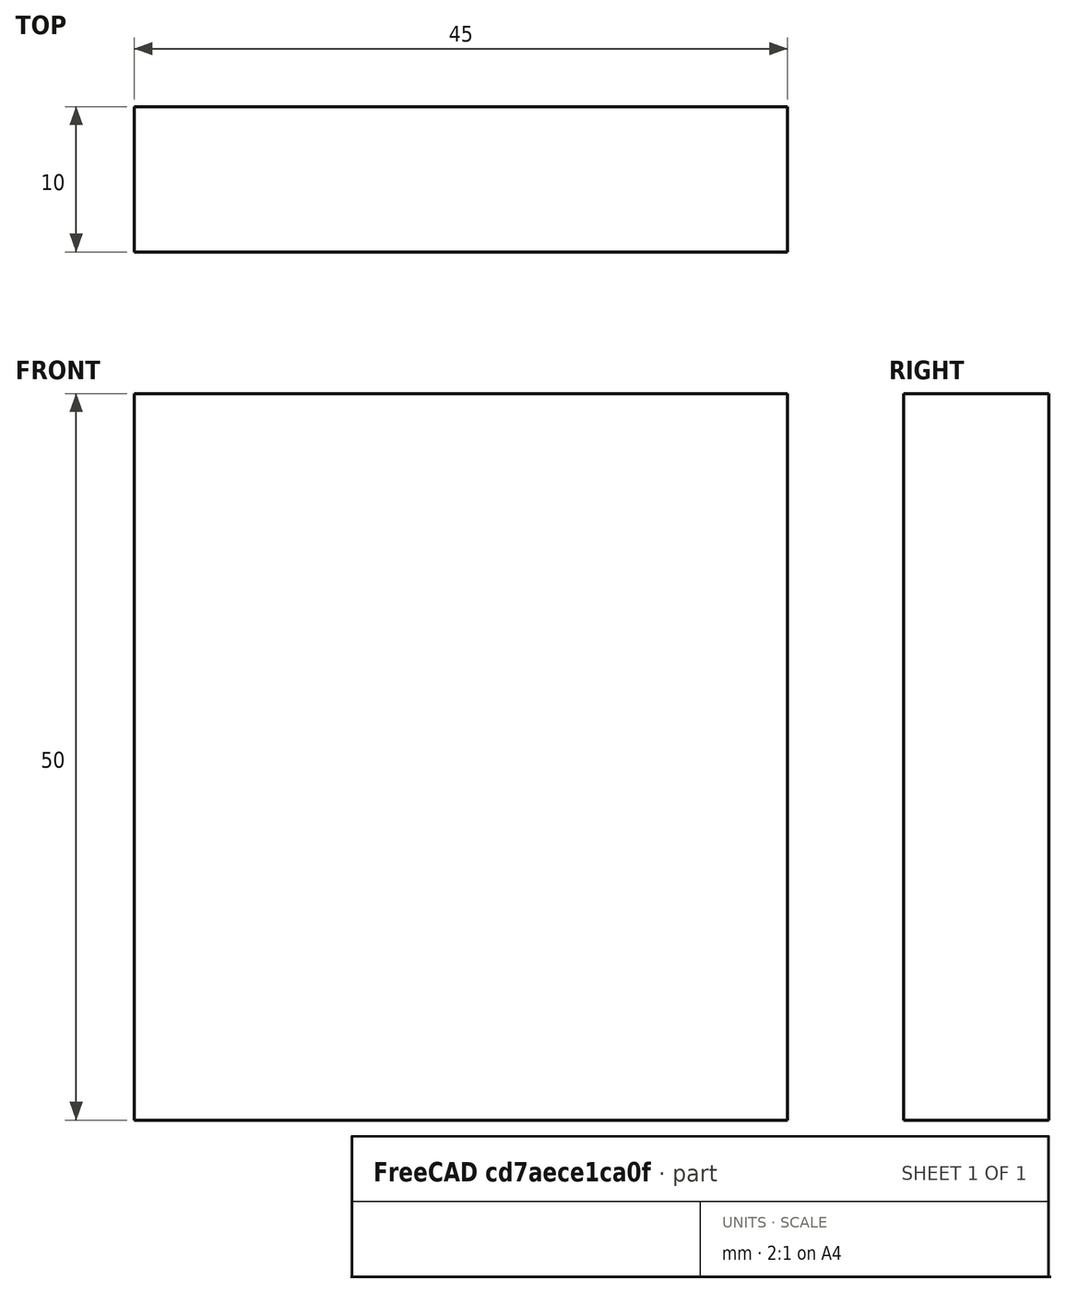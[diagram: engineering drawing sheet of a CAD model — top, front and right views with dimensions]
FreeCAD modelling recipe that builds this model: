
FCSTD DOCUMENT  (FreeCAD 0.15R4671 (Git))
Label: Flat Bar 45x10 EN10058 S235JR
License: All rights reserved
LicenseURL: http://en.wikipedia.org/wiki/All_rights_reserved
objects: Sketcher::SketchObject×1, Part::Extrusion×1
note: 2 computed .brp shape members not serialized (recipe doc carries the construction recipe); baked Part::Feature solids carry a one-line shape summary decoded from their .brp

FEATURE [Sketcher::SketchObject] Sketch
  sketch-geometry (4):
    g0: LineSegment StartX=-22.5 StartY=-5 StartZ=0 EndX=22.5 EndY=-5 EndZ=0
    g1: LineSegment StartX=22.5 StartY=-5 StartZ=0 EndX=22.5 EndY=5 EndZ=0
    g2: LineSegment StartX=22.5 StartY=5 StartZ=0 EndX=-22.5 EndY=5 EndZ=0
    g3: LineSegment StartX=-22.5 StartY=5 StartZ=0 EndX=-22.5 EndY=-5 EndZ=0
  constraints (12):
    c: Coincident(g0,g1)
    c: Coincident(g1,g2)
    c: Coincident(g2,g3)
    c: Coincident(g3,g0)
    c: Horizontal(g0)
    c: Horizontal(g2)
    c: Vertical(g1)
    c: Vertical(g3)
    c: Symmetric(g1,g2,g-2)
    c: Symmetric(g0,g1,g-1)
    c: DistanceY(g1) = 10
    c: DistanceX(g0) = 45
FEATURE [Part::Extrusion] Extrude  label="Flat Bar 45x10 EN10058 S235JR"
  Base = -> Sketch
  Dir = (0,0,50)
  Solid = true
